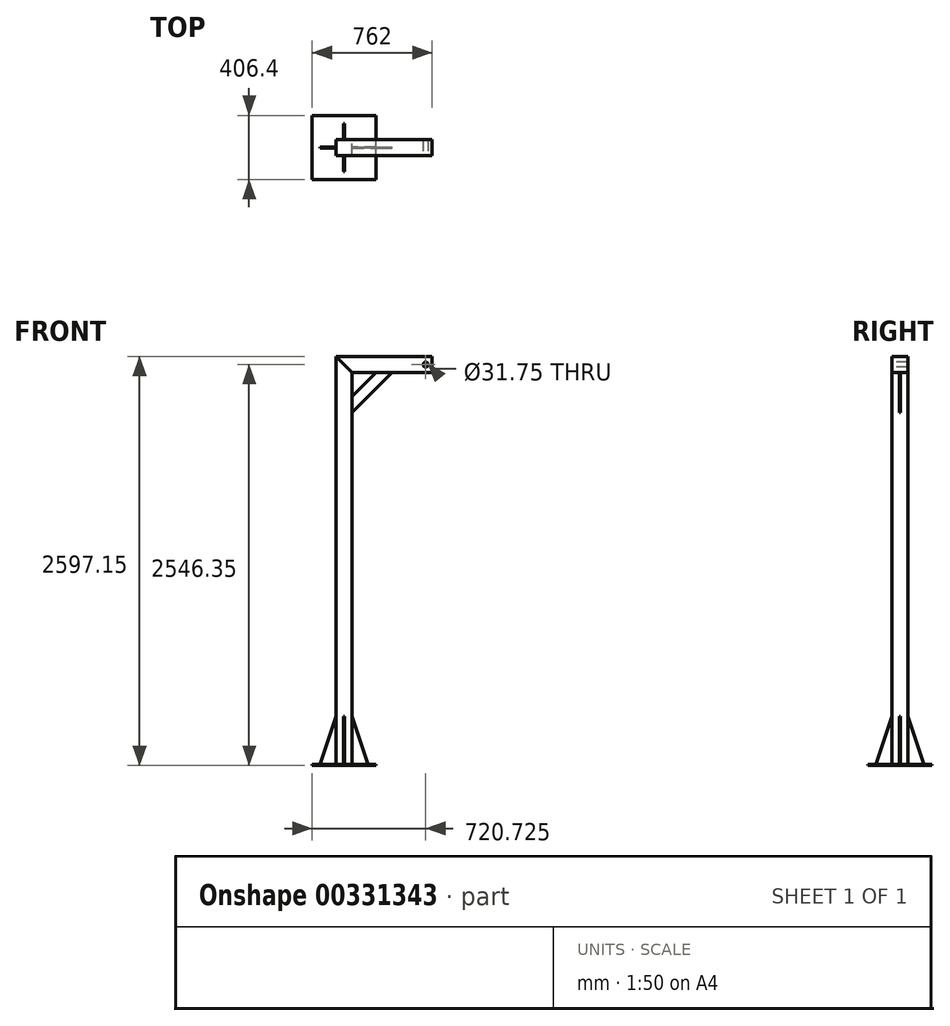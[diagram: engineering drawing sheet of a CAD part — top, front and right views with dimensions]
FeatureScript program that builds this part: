
annotation { "Feature Type Name" : "Feature", "Feature Type Description" : "" }
export const myFeature = defineFeature(function(context is Context, id is Id, definition is map)
    precondition{}
    {
        {
            var Q0;
            Q0=qCreatedBy(makeId("Front.planeOp"),FACE);
            var sketch = newSketch(context, id + "F0", { "sketchPlane" : qUnion([Q0])});
            skLineSegment(sketch, "E0.right", {"start": v(-50.8, 0) * mm, "end": v(-50.8, 2590.8) * mm});
            skPoint(sketch, "E0.bottom.start.orphan", {"position": v(-152.4, 0) * mm});
            skLineSegment(sketch, "E1", {"start": v(-50.8, 0) * mm, "end": v(50.8, 0) * mm});
            skLineSegment(sketch, "E2", {"start": v(50.8, 0) * mm, "end": v(50.8, 2590.8) * mm});
            skLineSegment(sketch, "E3", {"start": v(-50.8, 2590.8) * mm, "end": v(50.8, 2590.8) * mm});
            skLineSegment(sketch, "E4", {"start": v(-50.8, 2590.8) * mm, "end": v(50.8, 2489.2) * mm});
            skLineSegment(sketch, "E5", {"start": v(50.8, 2489.2) * mm, "end": v(50.8, 2590.8) * mm});
            skSolve(sketch);
        }
        {
            var Q0;
            Q0=makeQuery(id+"F0.imprint","IMPRINT",FACE,{"disambiguationData":[TD([[makeQuery(id+"F0.imprint","IMPRINT",EDGE,{"derivedFrom":sQuery(id+"F0.wireOp",EDGE,"E0.right")}),-1.0]])]});
            extrude(context, id + "F1", {"entities" : qUnion([Q0]), "endBound" : BoundingType.SYMMETRIC, "depth" : 101.6 * mm});
        }
        {
            var Q0;
            Q0=makeQuery(id+"F1.opExtrude","SWEPT_FACE",FACE,{"disambiguationData":[OSD([sQuery(id+"F0.wireOp",EDGE,"E1")])]});
            var sketch = newSketch(context, id + "F2", { "sketchPlane" : qUnion([Q0])});
            skLineSegment(sketch, "E6.bottom", {"start": v(-203.2, 203.2) * mm, "end": v(203.2, 203.2) * mm});
            skLineSegment(sketch, "E6.top", {"start": v(-203.2, -203.2) * mm, "end": v(203.2, -203.2) * mm});
            skLineSegment(sketch, "E6.left", {"start": v(-203.2, 203.2) * mm, "end": v(-203.2, -203.2) * mm});
            skLineSegment(sketch, "E6.right", {"start": v(203.2, 203.2) * mm, "end": v(203.2, -203.2) * mm});
            skSolve(sketch);
        }
        {
            var Q0;
            Q0 = qSketchRegion(id + "F2", true);
            extrude(context, id + "F3", {"entities" : qUnion([Q0]), "depth" : 6.35 * mm});
        }
        {
            var Q0;
            Q0=qCreatedBy(makeId("Front.planeOp"),FACE);
            var sketch = newSketch(context, id + "F4", { "sketchPlane" : qUnion([Q0])});
            skLineSegment(sketch, "E7", {"start": v(50.8, 304.8) * mm, "end": v(152.4, 0) * mm});
            skLineSegment(sketch, "E8", {"start": v(152.4, 0) * mm, "end": v(50.8, 0) * mm});
            skLineSegment(sketch, "E9", {"start": v(50.8, 0) * mm, "end": v(50.8, 304.8) * mm});
            skLineSegment(sketch, "E10", {"start": v(0, 2585.28) * mm, "end": v(0, -112.48) * mm, "construction": true});
            skLineSegment(sketch, "E11.MirrorCS", {"start": v(-50.8, 304.8) * mm, "end": v(-152.4, 0) * mm});
            skLineSegment(sketch, "E12.MirrorCS", {"start": v(-50.8, 0) * mm, "end": v(-50.8, 304.8) * mm});
            skLineSegment(sketch, "E13.MirrorCS", {"start": v(-152.4, 0) * mm, "end": v(-50.8, 0) * mm});
            skSolve(sketch);
        }
        {
            var Q0;
            Q0=qCreatedBy(makeId("Right.planeOp"),FACE);
            var sketch = newSketch(context, id + "F5", { "sketchPlane" : qUnion([Q0])});
            skLineSegment(sketch, "E14", {"start": v(50.8, 304.8) * mm, "end": v(152.4, 0) * mm});
            skLineSegment(sketch, "E15", {"start": v(152.4, 0) * mm, "end": v(50.8, 0) * mm});
            skLineSegment(sketch, "E16", {"start": v(50.8, 0) * mm, "end": v(50.8, 304.8) * mm});
            skLineSegment(sketch, "E17", {"start": v(0, 0) * mm, "end": v(0, 411.23) * mm, "construction": true});
            skLineSegment(sketch, "E18.MirrorCS", {"start": v(-50.8, 0) * mm, "end": v(-50.8, 304.8) * mm});
            skLineSegment(sketch, "E19.MirrorCS", {"start": v(-50.8, 304.8) * mm, "end": v(-152.4, 0) * mm});
            skLineSegment(sketch, "E20.MirrorCS", {"start": v(-152.4, 0) * mm, "end": v(-50.8, 0) * mm});
            skSolve(sketch);
        }
        {
            var Q0;
            Q0 = qSketchRegion(id + "F5", true);
            extrude(context, id + "F6", {"entities" : qUnion([Q0]), "endBound" : BoundingType.SYMMETRIC, "depth" : 6.35 * mm});
        }
        {
            var Q0;
            Q0 = qSketchRegion(id + "F4", true);
            extrude(context, id + "F7", {"entities" : qUnion([Q0]), "endBound" : BoundingType.SYMMETRIC, "depth" : 6.35 * mm});
        }
        {
            var Q0;
            Q0=makeQuery(id+"F0.imprint","IMPRINT",FACE,{"disambiguationData":[TD([[makeQuery(id+"F0.imprint","IMPRINT",EDGE,{"derivedFrom":sQuery(id+"F0.wireOp",EDGE,"E3")}),-1.0]])]});
            extrude(context, id + "F8", {"entities" : qUnion([Q0]), "operationType" : NewBodyOperationType.REMOVE, "endBound" : BoundingType.SYMMETRIC, "oppositeDirection" : true, "depth" : 101.6 * mm});
        }
        {
            var Q0;
            Q0=qCreatedBy(makeId("Front.planeOp"),FACE);
            var sketch = newSketch(context, id + "F9", { "sketchPlane" : qUnion([Q0])});
            skLineSegment(sketch, "E21", {"start": v(50.8, 2489.2) * mm, "end": v(558.8, 2489.2) * mm});
            skLineSegment(sketch, "E22", {"start": v(558.8, 2489.2) * mm, "end": v(558.8, 2590.8) * mm});
            skLineSegment(sketch, "E23", {"start": v(558.8, 2590.8) * mm, "end": v(-50.8, 2590.8) * mm});
            skLineSegment(sketch, "E24", {"start": v(-50.8, 2590.8) * mm, "end": v(50.8, 2489.2) * mm});
            skSolve(sketch);
        }
        {
            var Q0;
            Q0 = qSketchRegion(id + "F9", true);
            extrude(context, id + "F10", {"entities" : qUnion([Q0]), "endBound" : BoundingType.SYMMETRIC, "depth" : 101.6 * mm});
        }
        {
            var Q0;
            Q0=qCreatedBy(makeId("Front.planeOp"),FACE);
            var sketch = newSketch(context, id + "F11", { "sketchPlane" : qUnion([Q0])});
            skLineSegment(sketch, "E25", {"start": v(203.2, 2489.2) * mm, "end": v(50.8, 2336.8) * mm});
            skLineSegment(sketch, "E26", {"start": v(50.8, 2336.8) * mm, "end": v(50.8, 2489.2) * mm});
            skLineSegment(sketch, "E27", {"start": v(50.8, 2489.2) * mm, "end": v(203.2, 2489.2) * mm});
            skLineSegment(sketch, "E28", {"start": v(50.8, 2235.2) * mm, "end": v(304.8, 2489.2) * mm});
            skLineSegment(sketch, "E29", {"start": v(50.8, 2336.8) * mm, "end": v(50.8, 2235.2) * mm});
            skLineSegment(sketch, "E30", {"start": v(203.2, 2489.2) * mm, "end": v(304.8, 2489.2) * mm});
            skSolve(sketch);
        }
        {
            var Q0;
            Q0=makeQuery(id+"F11.imprint","IMPRINT",FACE,{"disambiguationData":[TD([[makeQuery(id+"F11.imprint","IMPRINT",EDGE,{"derivedFrom":sQuery(id+"F11.wireOp",EDGE,"E25")}),1.0]])]});
            extrude(context, id + "F12", {"entities" : qUnion([Q0]), "endBound" : BoundingType.SYMMETRIC, "depth" : 6.35 * mm});
        }
        {
            var Q0;
            Q0=makeQuery(id+"F10.opExtrude","CAP_FACE",FACE,{"disambiguationData":[OSD([sQuery(id+"F9.wireOp",EDGE,"E21"),sQuery(id+"F9.wireOp",EDGE,"E22"),sQuery(id+"F9.wireOp",EDGE,"E23"),sQuery(id+"F9.wireOp",EDGE,"E24")])],"isStart":false});
            var sketch = newSketch(context, id + "F13", { "sketchPlane" : qUnion([Q0])});
            skCircle(sketch, "E31", {"center": v(517.52, 2540) * mm, "radius": 15.88 * mm});
            skSolve(sketch);
        }
        {
            var Q0;
            Q0 = qSketchRegion(id + "F13", true);
            extrude(context, id + "F14", {"entities" : qUnion([Q0]), "operationType" : NewBodyOperationType.REMOVE, "oppositeDirection" : true, "depth" : 127 * mm});
        }
    });
